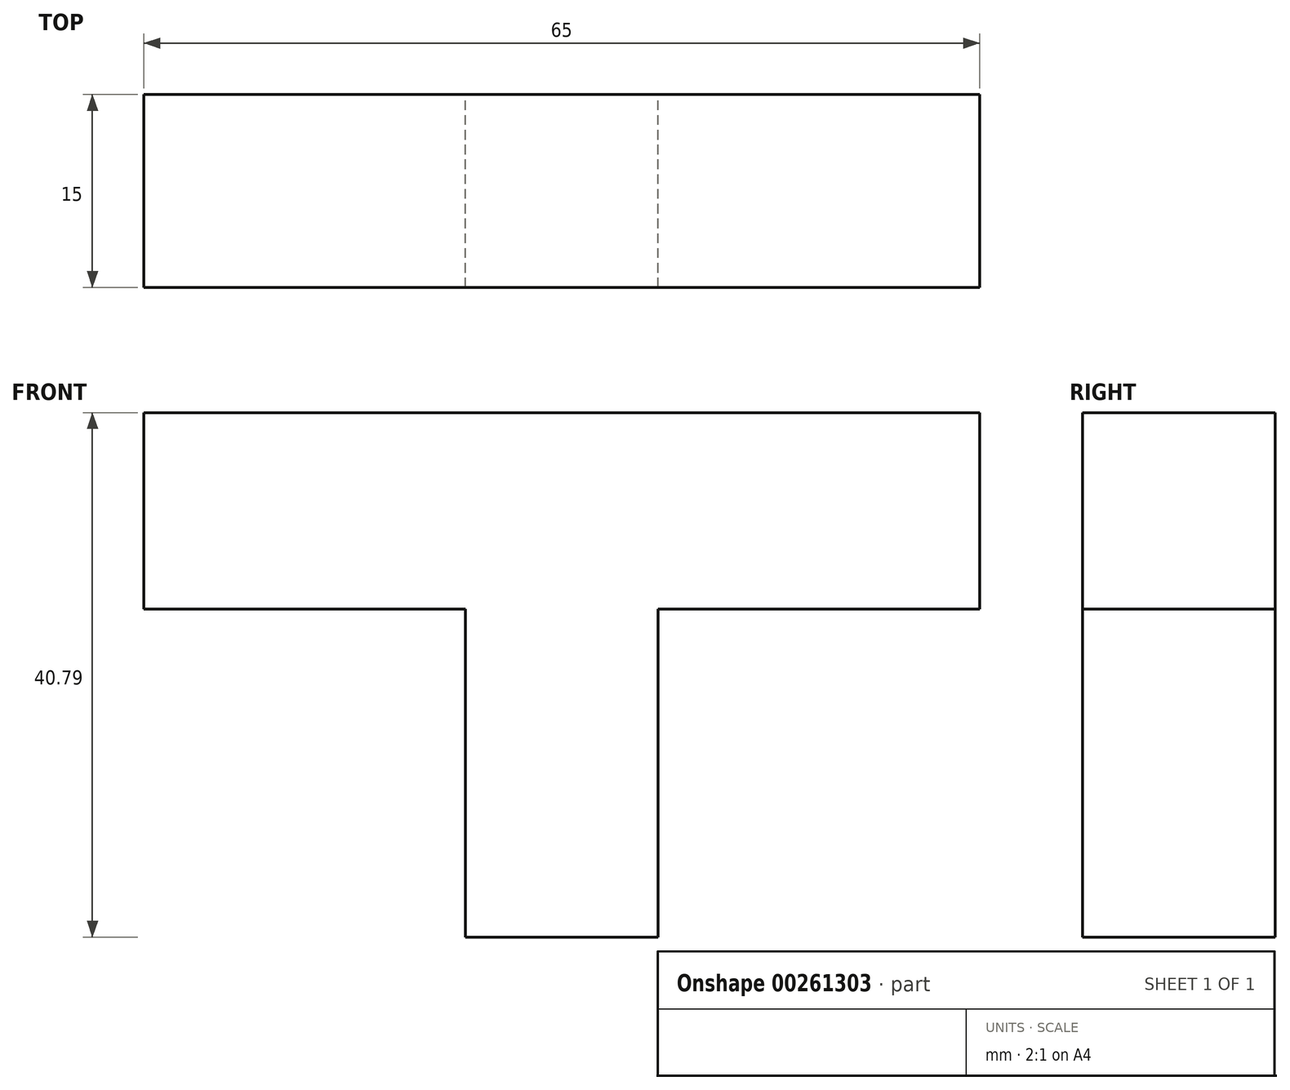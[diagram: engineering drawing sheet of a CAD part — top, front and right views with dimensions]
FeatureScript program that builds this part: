
annotation { "Feature Type Name" : "Feature", "Feature Type Description" : "" }
export const myFeature = defineFeature(function(context is Context, id is Id, definition is map)
    precondition{}
    {
        {
            var Q0;
            Q0=qCreatedBy(makeId("Front.planeOp"),FACE);
            var sketch = newSketch(context, id + "F0", { "sketchPlane" : qUnion([Q0])});
            skLineSegment(sketch, "E0", {"start": v(0, 0) * mm, "end": v(15, 0) * mm});
            skLineSegment(sketch, "E1", {"start": v(15, 0) * mm, "end": v(15, 25.53) * mm});
            skLineSegment(sketch, "E2", {"start": v(15, 25.53) * mm, "end": v(40, 25.53) * mm});
            skLineSegment(sketch, "E3", {"start": v(40, 40.79) * mm, "end": v(40, 25.53) * mm});
            skLineSegment(sketch, "E4", {"start": v(40, 40.79) * mm, "end": v(-25, 40.79) * mm});
            skLineSegment(sketch, "E5", {"start": v(-25, 40.79) * mm, "end": v(-25, 25.53) * mm});
            skLineSegment(sketch, "E6", {"start": v(-25, 25.53) * mm, "end": v(0, 25.53) * mm});
            skLineSegment(sketch, "E7", {"start": v(0, 25.53) * mm, "end": v(0, 0) * mm});
            skSolve(sketch);
        }
        {
            var Q0;
            Q0=makeQuery(id+"F0.imprint","IMPRINT",FACE,{"disambiguationData":[TD([[makeQuery(id+"F0.imprint","IMPRINT",EDGE,{"derivedFrom":sQuery(id+"F0.wireOp",EDGE,"E0")}),1.0]])]});
            extrude(context, id + "F1", {"entities" : qUnion([Q0]), "depth" : 15 * mm});
        }
    });
